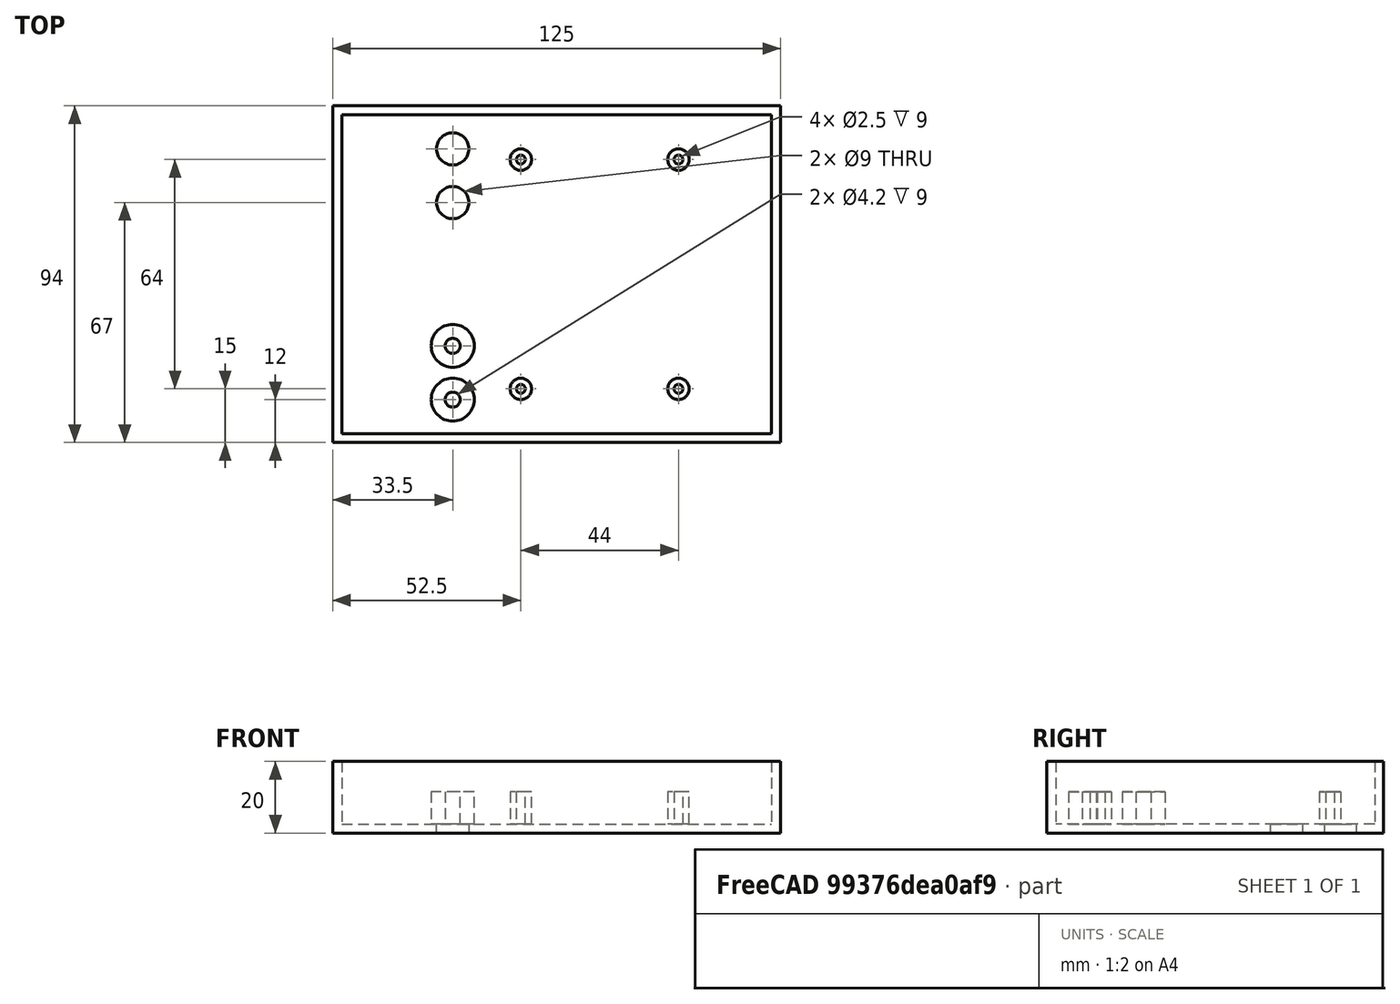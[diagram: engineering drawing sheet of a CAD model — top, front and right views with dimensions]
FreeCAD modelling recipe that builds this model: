
FCSTD DOCUMENT  (FreeCAD 0.19R24276 (Git))
Label: bottom
License: All rights reserved
LicenseURL: http://en.wikipedia.org/wiki/All_rights_reserved
objects: Sketcher::SketchObject×5, PartDesign::Pad×3, PartDesign::Plane×2, PartDesign::Pocket×2, Spreadsheet::Sheet×1, PartDesign::Mirrored×1, PartDesign::Body×1, Mesh::Feature×1
note: 19 computed .brp shape members not serialized (recipe doc carries the construction recipe); baked Part::Feature solids carry a one-line shape summary decoded from their .brp

FEATURE [Sketcher::SketchObject] Sketch
  FullyConstrained = true
  MapMode = 5
  Support = -> [XY_Plane]
  expr: Constraints[9] = <<Dimensions>>.length
  expr: Constraints[8] = <<Dimensions>>.width
  expr: Constraints[10] = <<Dimensions>>.width / 2
  expr: Constraints[11] = <<Dimensions>>.length / 2
  sketch-geometry (4):
    g0: LineSegment StartX=-62.5 StartY=47 StartZ=0 EndX=62.5 EndY=47 EndZ=0
    g1: LineSegment StartX=62.5 StartY=47 StartZ=0 EndX=62.5 EndY=-47 EndZ=0
    g2: LineSegment StartX=62.5 StartY=-47 StartZ=0 EndX=-62.5 EndY=-47 EndZ=0
    g3: LineSegment StartX=-62.5 StartY=-47 StartZ=0 EndX=-62.5 EndY=47 EndZ=0
  constraints (12):
    c: Coincident(g0,g1)
    c: Coincident(g1,g2)
    c: Coincident(g2,g3)
    c: Coincident(g3,g0)
    c: Horizontal(g0)
    c: Horizontal(g2)
    c: Vertical(g1)
    c: Vertical(g3)
    c: DistanceX(g0,g0) = 125
    c: DistanceY(g3,g3) = 94
    c: Distance(g-1,g1) = 62.5
    c: Distance(g-1,g0) = 47
FEATURE [PartDesign::Pad] Pad
  AllowMultiFace = false
  Direction = (1,1,1)
  Length = 20
  Length2 = 100
  Profile = -> Sketch
  Type = 0
  expr: Length = <<Dimensions>>.height
FEATURE [PartDesign::Plane] DatumPlane
  Length = 146.679
  MapMode = 5
  Placement = pos=(0,0,20) rot=(0,0,1;0rad)
  ResizeMode = 0
  Support = -> [Pad]
  Width = 115.679
FEATURE [Sketcher::SketchObject] Sketch001
  FullyConstrained = true
  MapMode = 5
  Placement = pos=(0,0,20) rot=(0,0,1;0rad)
  Support = -> [DatumPlane]
  expr: Constraints[8] = <<Dimensions>>.length - 2 * <<Dimensions>>.thickness
  expr: Constraints[9] = <<Dimensions>>.width - 2 * <<Dimensions>>.thickness
  expr: Constraints[10] = <<Dimensions>>.length / 2 - <<Dimensions>>.thickness
  expr: Constraints[11] = <<Dimensions>>.width / 2 - <<Dimensions>>.thickness
  sketch-geometry (4):
    g0: LineSegment StartX=-60 StartY=44.5 StartZ=0 EndX=60 EndY=44.5 EndZ=0
    g1: LineSegment StartX=60 StartY=44.5 StartZ=0 EndX=60 EndY=-44.5 EndZ=0
    g2: LineSegment StartX=60 StartY=-44.5 StartZ=0 EndX=-60 EndY=-44.5 EndZ=0
    g3: LineSegment StartX=-60 StartY=-44.5 StartZ=0 EndX=-60 EndY=44.5 EndZ=0
  constraints (12):
    c: Coincident(g0,g1)
    c: Coincident(g1,g2)
    c: Coincident(g2,g3)
    c: Coincident(g3,g0)
    c: Horizontal(g0)
    c: Horizontal(g2)
    c: Vertical(g1)
    c: Vertical(g3)
    c: DistanceY(g1,g1) = 89
    c: DistanceX(g0,g0) = 120
    c: Distance(g-1,g0) = 44.5
    c: Distance(g-1,g3) = 60
FEATURE [PartDesign::Pocket] Pocket
  AllowMultiFace = false
  BaseFeature = -> Pad
  Length = 17.5
  Length2 = 100
  Profile = -> Sketch001
  Type = 0
  expr: Length = <<Dimensions>>.height - <<Dimensions>>.thickness
FEATURE [PartDesign::Plane] DatumPlane001
  Length = 146.679
  MapMode = 5
  Placement = pos=(0,0,2.5) rot=(0,0,1;0rad)
  ResizeMode = 0
  Support = -> [Pocket]
  Width = 115.679
FEATURE [Sketcher::SketchObject] Sketch002
  FullyConstrained = false
  MapMode = 5
  Placement = pos=(0,0,2.5) rot=(0,0,1;0rad)
  Support = -> [DatumPlane001]
  expr: Constraints[10] = 4.2 / 2
  sketch-geometry (5):
    g0: Circle CenterX=-29 CenterY=-35 CenterZ=0 NormalX=0 NormalY=0 NormalZ=1 AngleXU=0 Radius=6
    g1: Circle CenterX=-29 CenterY=-20 CenterZ=0 NormalX=0 NormalY=0 NormalZ=1 AngleXU=0 Radius=6
    g2: Circle CenterX=-29 CenterY=-20 CenterZ=0 NormalX=0 NormalY=0 NormalZ=1 AngleXU=0 Radius=2.1
    g3: Circle CenterX=-29 CenterY=-35 CenterZ=0 NormalX=0 NormalY=0 NormalZ=1 AngleXU=0 Radius=2.1
    g4: LineSegment StartX=-29 StartY=-15.3882 StartZ=0 EndX=-29 EndY=-41.3739 EndZ=0
  constraints (11):
    c: Radius(g0) = 6
    c: Equal(g1,g0)
    c: Distance(g1,g0) = 15
    c: Coincident(g2,g1)
    c: Coincident(g3,g0)
    c: Equal(g2,g3)
    c: Distance(g0,g-1) = 35
    c: Vertical(g4)
    c: PointOnObject(g1,g4)
    c: PointOnObject(g0,g4)
    c: Radius(g2) = 2.1
FEATURE [PartDesign::Pad] Pad001
  AllowMultiFace = false
  BaseFeature = -> Pocket
  Direction = (1,1,1)
  Length = 9
  Length2 = 100
  Profile = -> Sketch002
  Type = 0
FEATURE [Spreadsheet::Sheet] Spreadsheet  label="Dimensions"
  cells = A1=Width; B1(width)==125mm; A2=Length; B2(length)==94mm; A3=Thickness; B3(thickness)==2.5mm; A4=Height; B4(height)==20mm; A5=Standoff offset; B5(standoff_offset)==29mm
FEATURE [Sketcher::SketchObject] Sketch003
  FullyConstrained = false
  MapMode = 5
  Placement = pos=(0,0,2.5) rot=(0,0,1;0rad)
  Support = -> [DatumPlane001]
  expr: Constraints[8] = 64 / 2
  sketch-geometry (5):
    g0: Circle CenterX=-10 CenterY=32 CenterZ=0 NormalX=0 NormalY=0 NormalZ=1 AngleXU=0 Radius=1.25
    g1: Circle CenterX=-10 CenterY=32 CenterZ=0 NormalX=0 NormalY=0 NormalZ=1 AngleXU=0 Radius=3
    g2: Circle CenterX=34 CenterY=32 CenterZ=0 NormalX=0 NormalY=0 NormalZ=1 AngleXU=0 Radius=1.25
    g3: Circle CenterX=34 CenterY=32 CenterZ=0 NormalX=0 NormalY=0 NormalZ=1 AngleXU=0 Radius=3
    g4: LineSegment StartX=-19.406 StartY=32 StartZ=0 EndX=38.1652 EndY=32 EndZ=0
  constraints (12):
    c: Radius(g0) = 1.25
    c: Coincident(g1,g0)
    c: Radius(g1) = 3
    c: Distance(g0,g-2) = 10
    c: Coincident(g3,g2)
    c: Horizontal(g4)
    c: PointOnObject(g0,g4)
    c: PointOnObject(g2,g4)
    c: Distance(g-1,g4) = 32
    c: Distance(g0,g2) = 44
    c: Equal(g0,g2)
    c: Equal(g1,g3)
FEATURE [PartDesign::Pad] Pad002
  BaseFeature = -> Pad001
  Direction = (1,1,1)
  Length = 9
  Length2 = 100
  Profile = -> Sketch003
  Type = 0
FEATURE [PartDesign::Mirrored] Mirrored
  BaseFeature = -> Pad002
  MirrorPlane = -> Sketch003 [H_Axis]
  Originals = -> [Pad002]
FEATURE [Sketcher::SketchObject] Sketch004
  FullyConstrained = true
  MapMode = 5
  Placement = pos=(0,0,2.5) rot=(0,0,1;0rad)
  Support = -> [DatumPlane001]
  expr: Constraints[4] = 9 / 2
  expr: Constraints[0] = <<Dimensions>>.standoff_offset
  sketch-geometry (2):
    g0: Circle CenterX=-29 CenterY=35 CenterZ=0 NormalX=0 NormalY=0 NormalZ=1 AngleXU=0 Radius=4.5
    g1: Circle CenterX=-29 CenterY=20 CenterZ=0 NormalX=0 NormalY=0 NormalZ=1 AngleXU=0 Radius=4.5
  constraints (6):
    c: Distance(g0,g-2) = 29
    c: Distance(g0,g-1) = 35
    c: Distance(g1,g-2) = 29
    c: Distance(g0,g1) = 15
    c: Radius(g0) = 4.5
    c: Equal(g1,g0)
FEATURE [PartDesign::Pocket] Pocket001
  BaseFeature = -> Mirrored
  Length = 5
  Length2 = 100
  Profile = -> Sketch004
  Type = 1
FEATURE [PartDesign::Body] Body
  Group = -> [Sketch,Pad,DatumPlane,Sketch001,Pocket,DatumPlane001,Sketch002,Pad001,Sketch003,Pad002,Mirrored,Sketch004,Pocket001]
  Origin = -> Origin
  Tip = -> Pocket001
FEATURE [Mesh::Feature] Mesh  label="Body (Meshed)"
